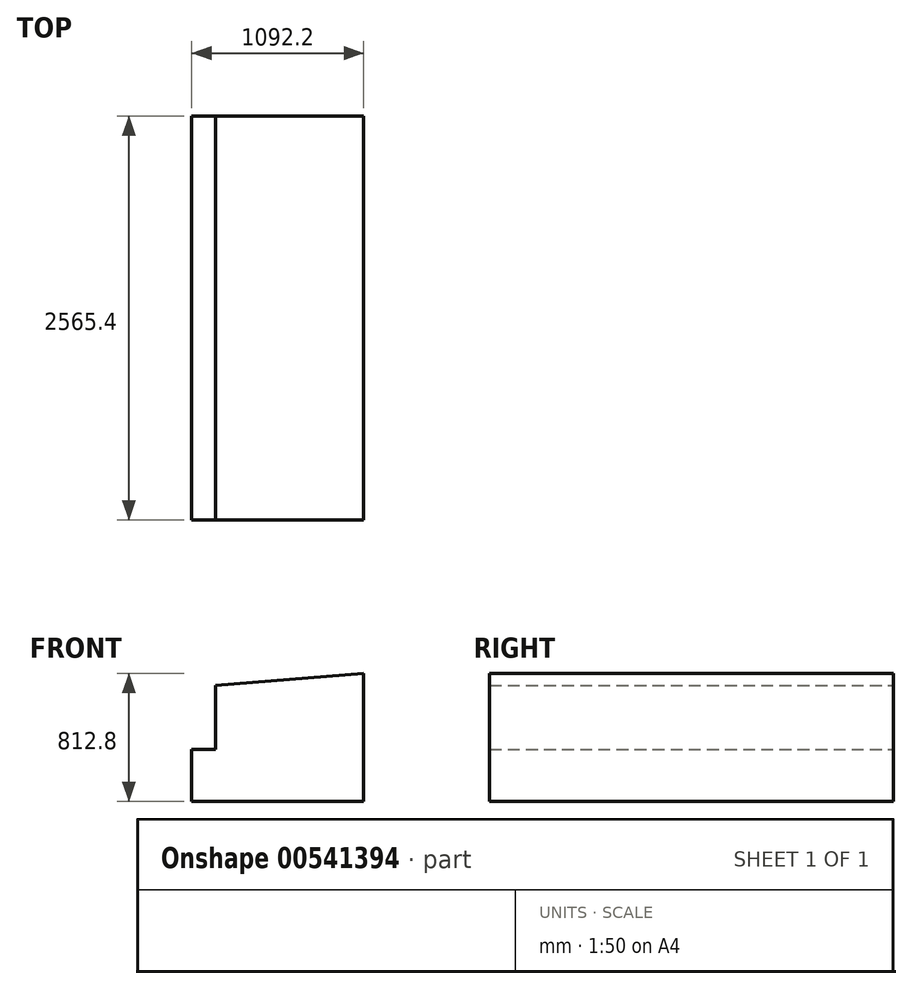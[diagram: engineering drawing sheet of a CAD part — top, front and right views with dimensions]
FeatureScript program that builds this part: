
annotation { "Feature Type Name" : "Feature", "Feature Type Description" : "" }
export const myFeature = defineFeature(function(context is Context, id is Id, definition is map)
    precondition{}
    {
        {
            var Q0;
            Q0=qCreatedBy(makeId("Front.planeOp"),FACE);
            var sketch = newSketch(context, id + "F0", { "sketchPlane" : qUnion([Q0])});
            skLineSegment(sketch, "E0", {"start": v(1092.2, 812.8) * mm, "end": v(152.4, 736.6) * mm});
            skLineSegment(sketch, "E1", {"start": v(152.4, 736.6) * mm, "end": v(152.4, 330.2) * mm});
            skLineSegment(sketch, "E2", {"start": v(152.4, 330.2) * mm, "end": v(0, 330.2) * mm});
            skLineSegment(sketch, "E3", {"start": v(0, 330.2) * mm, "end": v(0, 0) * mm});
            skLineSegment(sketch, "E4", {"start": v(0, 0) * mm, "end": v(1092.2, 0) * mm});
            skLineSegment(sketch, "E5", {"start": v(1092.2, 812.8) * mm, "end": v(1092.2, 0) * mm});
            skLineSegment(sketch, "E6", {"start": v(0, 76.2) * mm, "end": v(1092.2, 76.2) * mm, "construction": true});
            skLineSegment(sketch, "E7", {"start": v(152.4, 736.6) * mm, "end": v(1092.2, 76.2) * mm, "construction": true});
            skLineSegment(sketch, "E8", {"start": v(152.4, 736.6) * mm, "end": v(1092.2, 0) * mm, "construction": true});
            skLineSegment(sketch, "E9", {"start": v(152.4, 330.2) * mm, "end": v(939.8, 330.2) * mm, "construction": true});
            skLineSegment(sketch, "E10", {"start": v(939.8, 330.2) * mm, "end": v(939.8, 800.44) * mm, "construction": true});
            skLineSegment(sketch, "E11", {"start": v(0, 330.2) * mm, "end": v(939.8, 800.44) * mm, "construction": true});
            skLineSegment(sketch, "E12", {"start": v(1092.2, 0) * mm, "end": v(741.37, 701.15) * mm, "construction": true});
            skLineSegment(sketch, "E13", {"start": v(1092.2, 76.2) * mm, "end": v(771.86, 716.41) * mm, "construction": true});
            skSolve(sketch);
        }
        {
            var Q0;
            Q0 = qSketchRegion(id + "F0", true);
            extrude(context, id + "F1", {"entities" : qUnion([Q0]), "depth" : 2565.4 * mm, "offsetDistance" : 25.4 * mm});
        }
    });
